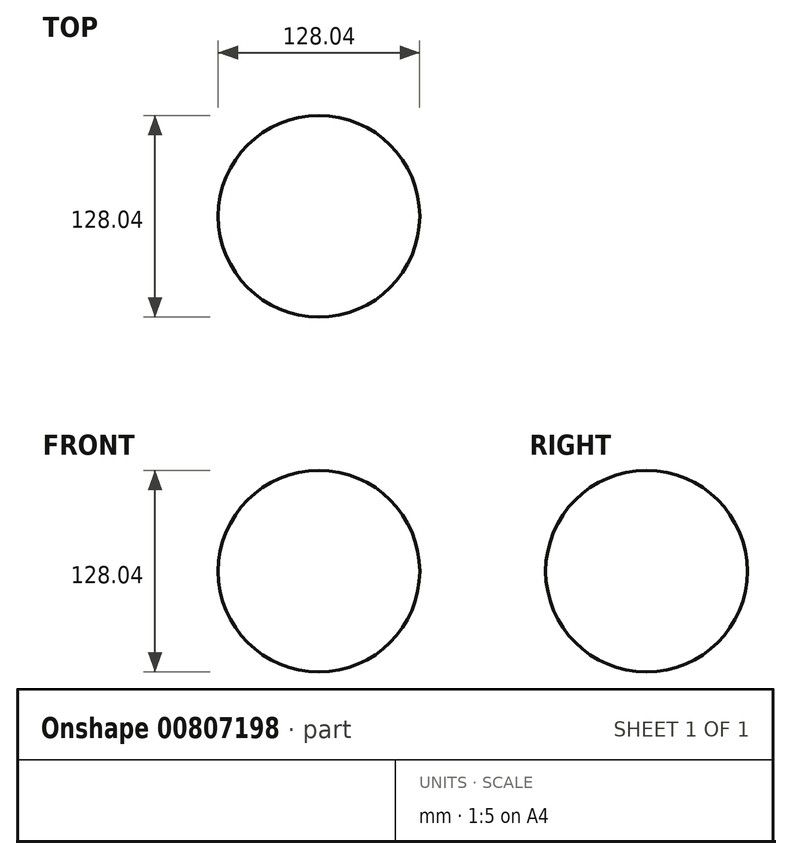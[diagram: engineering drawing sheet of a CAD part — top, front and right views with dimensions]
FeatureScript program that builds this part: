
annotation { "Feature Type Name" : "Feature", "Feature Type Description" : "" }
export const myFeature = defineFeature(function(context is Context, id is Id, definition is map)
    precondition{}
    {
        {
            var Q0;
            Q0=qCreatedBy(makeId("Front.planeOp"),FACE);
            var sketch = newSketch(context, id + "F0", { "sketchPlane" : qUnion([Q0])});
            skCircle(sketch, "E0", {"center": v(0, -2.48) * mm, "radius": 64.02 * mm});
            skLineSegment(sketch, "E1", {"start": v(0, -2.48) * mm, "end": v(0, 113.13) * mm});
            skLineSegment(sketch, "E2", {"start": v(0, 113.13) * mm, "end": v(0, -114.57) * mm});
            skSolve(sketch);
        }
        {
            var Q0;
            {var subQ0=sQuery(id+"F0.wireOp",EDGE,"E1");var subQ1=sQuery(id+"F0.wireOp",EDGE,"E0");var subQ2=makeQuery(id+"F0.imprint","INTERSECT",VERTEX,{"derivedFrom":[subQ1,subQ0]});Q0=makeQuery(id+"F0.imprint","IMPRINT",FACE,{"disambiguationData":[TD([[makeQuery(id+"F0.imprint","IMPRINT",EDGE,{"disambiguationData":[TD([[subQ2,1.0]])],"derivedFrom":subQ1}),1.0]])]});}
            var Q1;
            Q1=sQuery(id+"F0.wireOp",EDGE,"E2");
            revolve(context, id + "F1", {"surfaceOperationType" : NewSurfaceOperationType.NEW, "entities" : qUnion([Q0]), "axis" : qUnion([Q1]), "revolveType" : RevolveType.FULL});
        }
    });
